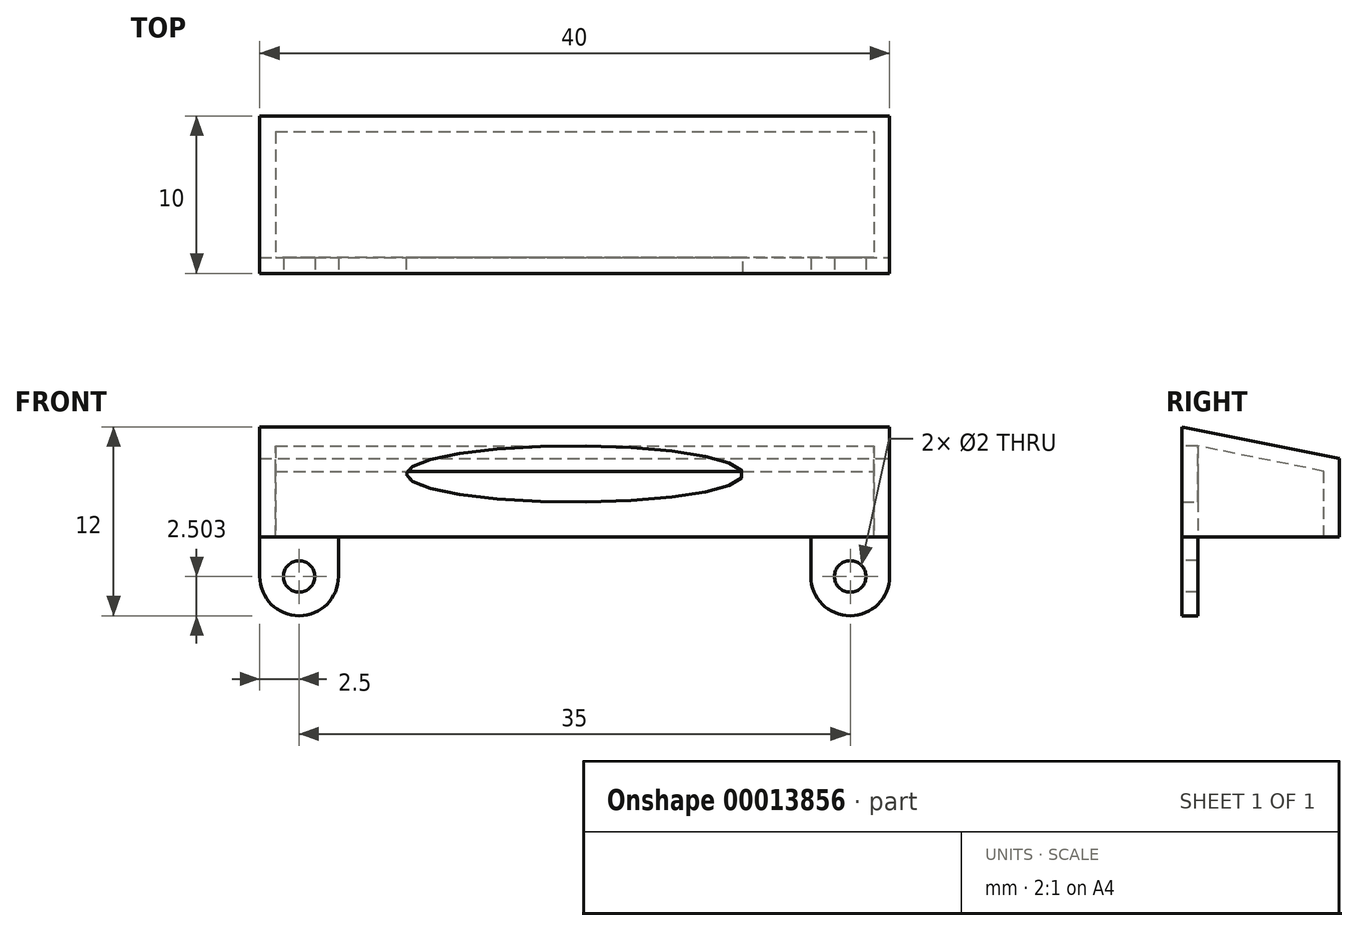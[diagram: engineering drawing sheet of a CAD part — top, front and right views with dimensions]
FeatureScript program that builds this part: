
annotation { "Feature Type Name" : "Feature", "Feature Type Description" : "" }
export const myFeature = defineFeature(function(context is Context, id is Id, definition is map)
    precondition{}
    {
        {
            var Q0;
            Q0=qCreatedBy(makeId("Right.planeOp"),FACE);
            var sketch = newSketch(context, id + "F0", { "sketchPlane" : qUnion([Q0])});
            skLineSegment(sketch, "E0.top", {"start": v(-22.25, 38.36) * mm, "end": v(-12.25, 38.36) * mm});
            skLineSegment(sketch, "E0.left", {"start": v(-22.25, 45.36) * mm, "end": v(-22.25, 38.36) * mm});
            skLineSegment(sketch, "E0.right", {"start": v(-12.25, 43.36) * mm, "end": v(-12.25, 38.36) * mm});
            skLineSegment(sketch, "E1.left", {"start": v(-12.25, 38.36) * mm, "end": v(-12.25, 43.36) * mm});
            skLineSegment(sketch, "E2", {"start": v(-12.25, 43.36) * mm, "end": v(-22.25, 45.36) * mm});
            skSolve(sketch);
        }
        {
            var Q0;
            Q0=makeQuery(id+"F0.imprint","IMPRINT",FACE,{"disambiguationData":[TD([[makeQuery(id+"F0.imprint","IMPRINT",EDGE,{"derivedFrom":sQuery(id+"F0.wireOp",EDGE,"E0.top")}),1.0]])]});
            extrude(context, id + "F1", {"entities" : qUnion([Q0]), "oppositeDirection" : true, "depth" : 40 * mm});
        }
        {
            var Q0;
            Q0=makeQuery(id+"F1.opExtrude","CAP_FACE",FACE,{"disambiguationData":[OSD([sQuery(id+"F0.wireOp",EDGE,"E0.top"),sQuery(id+"F0.wireOp",EDGE,"E0.left"),sQuery(id+"F0.wireOp",EDGE,"E1.left"),sQuery(id+"F0.wireOp",EDGE,"E2")])],"isStart":true});
            cPlane(context, id + "F2", {"entities" : qUnion([Q0]), "cplaneType" : CPlaneType.OFFSET, "offset" : 1 * mm, "oppositeDirection" : true, "width" : 150 * mm, "height" : 150 * mm});
        }
        {
            var Q0;
            Q0=qCreatedBy(id+"F2.planeOp",FACE);
            var sketch = newSketch(context, id + "F3", { "sketchPlane" : qUnion([Q0])});
            skLineSegment(sketch, "E3.0", {"start": v(-21.25, 44.14) * mm, "end": v(-21.25, 34.6) * mm});
            skLineSegment(sketch, "E3.1", {"start": v(-13.25, 42.54) * mm, "end": v(-21.25, 44.14) * mm});
            skLineSegment(sketch, "E3.2", {"start": v(-13.25, 34.6) * mm, "end": v(-13.25, 42.54) * mm});
            skLineSegment(sketch, "E4", {"start": v(-21.25, 34.6) * mm, "end": v(-13.25, 34.6) * mm});
            skSolve(sketch);
        }
        {
            var Q0;
            Q0 = qSketchRegion(id + "F3", true);
            extrude(context, id + "F4", {"entities" : qUnion([Q0]), "operationType" : NewBodyOperationType.REMOVE, "oppositeDirection" : true, "depth" : 38 * mm});
        }
        {
            var Q0;
            Q0=makeQuery(id+"F1.opExtrude","SWEPT_FACE",FACE,{"disambiguationData":[OSD([sQuery(id+"F0.wireOp",EDGE,"E0.left")])]});
            var sketch = newSketch(context, id + "F5", { "sketchPlane" : qUnion([Q0])});
            skLineSegment(sketch, "E5.0", {"start": v(-40, 38.36) * mm, "end": v(0, 38.36) * mm});
            skCircle(sketch, "E6", {"center": v(-37.5, 35.86) * mm, "radius": 1 * mm});
            skCircle(sketch, "E7", {"center": v(-2.5, 35.86) * mm, "radius": 1 * mm});
            skArc(sketch, "E8", {"start": v(-40, 35.86) * mm, "mid": v(-37.5, 33.36) * mm, "end": v(-35, 35.86) * mm});
            skArc(sketch, "E9", {"start": v(-5, 35.86) * mm, "mid": v(-2.5, 33.36) * mm, "end": v(0, 35.86) * mm});
            skLineSegment(sketch, "E10", {"start": v(-40, 38.36) * mm, "end": v(-40, 35.86) * mm});
            skLineSegment(sketch, "E11", {"start": v(0, 38.36) * mm, "end": v(0, 35.86) * mm});
            skLineSegment(sketch, "E12", {"start": v(-35, 38.36) * mm, "end": v(-35, 35.86) * mm});
            skLineSegment(sketch, "E13", {"start": v(-5, 38.36) * mm, "end": v(-5, 35.86) * mm});
            skSolve(sketch);
        }
        {
            var Q0;
            Q0 = qSketchRegion(id + "F5", true);
            extrude(context, id + "F6", {"entities" : qUnion([Q0]), "oppositeDirection" : true, "depth" : 1 * mm});
        }
        {
            var Q0;
            Q0=makeQuery(id+"F1.opExtrude","SWEPT_FACE",FACE,{"disambiguationData":[OSD([sQuery(id+"F0.wireOp",EDGE,"E0.left")])]});
            var sketch = newSketch(context, id + "F7", { "sketchPlane" : qUnion([Q0])});
            skEllipse(sketch, "E14", {"center": v(-20, 42.36) * mm, "majorRadius": 10.7 * mm, "minorRadius": 1.78 * mm, "majorAxis": v(-1, 0)});
            skSolve(sketch);
        }
        {
            var Q0;
            Q0 = qSketchRegion(id + "F7", true);
            extrude(context, id + "F8", {"entities" : qUnion([Q0]), "operationType" : NewBodyOperationType.REMOVE, "oppositeDirection" : true, "depth" : 1 * mm});
        }
    });
